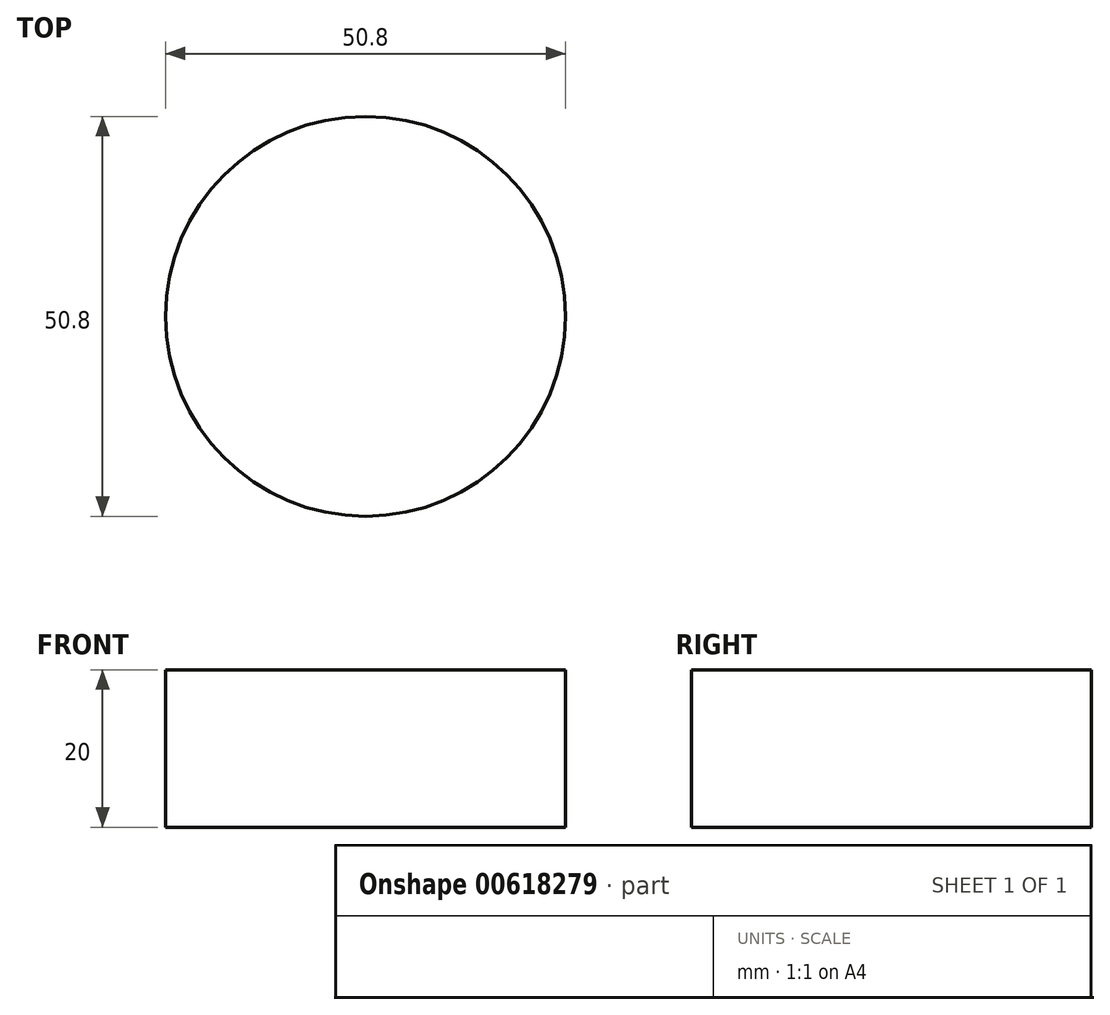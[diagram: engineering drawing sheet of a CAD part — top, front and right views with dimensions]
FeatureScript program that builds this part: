
annotation { "Feature Type Name" : "Feature", "Feature Type Description" : "" }
export const myFeature = defineFeature(function(context is Context, id is Id, definition is map)
    precondition{}
    {
        {
            var Q0;
            Q0=qCreatedBy(makeId("Top.planeOp"),FACE);
            var sketch = newSketch(context, id + "F0", { "sketchPlane" : qUnion([Q0])});
            skCircle(sketch, "E0", {"center": v(0, 0) * mm, "radius": 25.4 * mm});
            skSolve(sketch);
        }
        {
            var Q0;
            Q0 = qSketchRegion(id + "F0", true);
            extrude(context, id + "F1", {"entities" : qUnion([Q0]), "depth" : 20 * mm, "offsetDistance" : 25 * mm});
        }
    });
